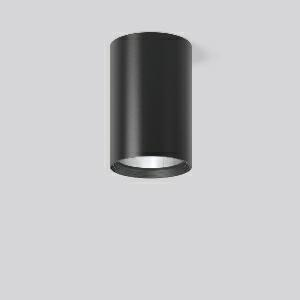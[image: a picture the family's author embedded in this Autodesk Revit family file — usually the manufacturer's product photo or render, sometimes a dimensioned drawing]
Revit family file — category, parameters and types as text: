
# Revit family: heledon_maxi_a_931225_003_1_6b55
name_source: partatom
category: Lighting Fixtures
units: mm (PartAtom-declared; Revit-internal decimal feet)

## family parameters
Cut with Voids When Loaded = No
Host = Face
Light Source = No
Part Type = Normal
Room Calculation Point = No
Round Connector Dimension = Use Diameter
Shared = No

## types (1)
- HELEDON maxi A (1 x LED Modul 940, 4550 lm, 4000)
    Apparent Load = 35 VA
    Approval mark = CE
    CIE Flux Codes = 100 100 100 100 100
    Color Rendering = 92
    Color Temperature = 4000
    Default Elevation = 1800 mm
    Description = Series: HELEDON maxi
Cylindrical surface-mounted downlight. Housing: die-cast aluminium, powder-coated. Internal ceiling frame polycarbonate with bayonet mounting. Black plastic ring and recessed LED to prevent glare from the side. Optical assembly with reflector made of MIRO-Silver with 98% total light reflection for outstanding efficiency - can be changed without tools. Best colour rendering index Ra>90. Suitable for Ceiling mounting. Easy installation with a separate ceiling frame with bayonet mounting and plug connection. Driver integrated. Connected via plug-in connector. High quality converter without flickering and stroboscopic effect. The following accessories can be mounted without use of tools: interchangeable lenses, decorative glasses, honeycomb louvre, clear and frosted diffusers, white interchangeable plastic ring. 
Colour: deep black, matt (RAL 9005)
Diameter: 123 mm
Height: 183 mm
Lamp: LED
Socket: without socket
Colour temperature: 4000K
Colour rendering index (CRI): 92
System power: 35 W
Rated luminous flux: 4550 lm
Luminous efficiency: 130 lm/W
Control gear: Regulated power supply
Protection class: I
Type of protection: IP 20
    Height = 183 mm
    Lamp = 1 x LED Modul 940
    Lamp Light Flux = 4550 lm
    Lamp count = 1
    Length = 123 mm
    Lifetime = 50000 h
    Luminous efficacy = 130 lm/W
    Manufacturer = RZB
    ModVariant = No
    Model = 931225.003.1
    Mounting Place = Ceiling
    Mounting Type = Surface mounted
    Number of Poles = 1
    OnlyDefault = Yes
    Power Factor = 1
    Product Name = HELEDON maxi A
    Product group = Surface mounted downlights
    ProductGroupID = 302
    Protection Class = Protection class I
    Protection Degree = IP 20
    RLX_Detail_Level = 1
    RLX_Emergency_Light_Flux = 0 lm
    RLX_Emergency_Type = 0
    RLX_Emergency_Type_DB = No
    RlxData = <blob elided: 96541 chars, md5=e049882f>
    Socket = socket
    Standby Power = 0 W
    System Light Flux = 4550 lm
    System Power = 35 W
    Type Comments = Product without accessories
    Type Image = 931192.003.jpg
    URL = http://relux.com
    VarID = ---
    Voltage = 230 V
    Voltage Range = 220-240 V
    Weight = 0.00 kg
    Width = 0 mm  [stored 0 ft]

note: [stored X ft] marks values corroborated as IEEE doubles in the binary element streams (Revit-internal decimal feet)

## geometry (parser evidence)
native form markers: Blend x4, Sweep x10
no freeform markers — native parametric forms only
